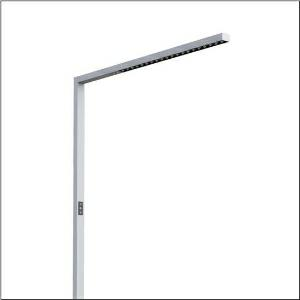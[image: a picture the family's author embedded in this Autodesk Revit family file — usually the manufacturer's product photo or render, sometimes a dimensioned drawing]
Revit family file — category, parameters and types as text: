
# Revit family: silica_31_floor_51my52fa4cs
name_source: partatom
category: Lighting Fixtures
units: mm (PartAtom-declared; Revit-internal decimal feet)

## family parameters
Cut with Voids When Loaded = No
Host = Face
Light Source = No
Part Type = Normal
Room Calculation Point = No
Round Connector Dimension = Use Diameter
Shared = No

## types (1)
- Silica 31 Floor (1 x LED, 10600 lm, 75 W, 4000K)
    Apparent Load = 75 VA
    CIE Flux Codes = 86 100 100 24 100
    Color Rendering = 80
    Color Temperature = 4000K
    Default Elevation = 1800 mm
    Description = Silica® 31 Floor, floorstanding luminaire, secondary optical cover: cover panel, of PMMA, light emission: direct/indirect distribution, primary light characteristic: symmetric, installation type: not mounted, LED, rated luminous flux: 10.600lm, luminous efficacy: 141lm/W, light colour: 840, colour temperature: 4000K, control gear: Touchdim, daylight-dependent control, with cable with plug, mains connection: 230V, AC, 50Hz, connection cable included, cable length: 2,5m, rated input power: 75W, luminaire head, of aluminium, metallic grey (RAL 9006), length: 1.203mm, width: 52mm, supporting column, angular, of aluminium, metallic grey (RAL 9006), baseplate, of steel, metallic grey (RAL 9006), local control - self-sufficient standalone sensors, direct and indirect component separately switchable, protection rating (complete): IP20, insulation class (complete): insulation class I (protective earthing), certification: CE, ENEC, permissible operating ambient temperature: -20..+40°C, standard: EN 50419, packaging unit: 1 piece
    Height = 36 mm
    Lamp = 1 x LED
    Lamp Light Flux = 10600 lm
    Lamp Power = 75 W
    Lamp count = 1
    Length = 1203 mm
    Luminous efficacy = 141 lm/W
    Manufacturer = Siteco
    ModVariant = No
    Model = 51MY52FA4CS
    Mounting Place = Floor
    Mounting Type = Freestanding
    Number of Poles = 1
    OnlyDefault = Yes
    Power Factor = 1
    Product Name = Silica 31 Floor
    Product group = floorstanding luminaire
    ProductGroupID = 1302
    Protection Class = Protection class I
    Protection Degree = IP 20
    RLX_Detail_Level = 1
    RLX_Emergency_Light_Flux = 0 lm
    RLX_Emergency_Type = 0
    RLX_Emergency_Type_DB = No
    RlxData = <blob elided: 19733 chars, md5=68699f00>
    Socket = socket
    Standby Power = 0 W
    System Light Flux = 10600 lm
    System Power = 75 W
    Type Comments = Product without accessories
    Type Image = l_1275303.jpg
    URL = http://relux.com
    VarID = ---
    Voltage = 0 V
    Weight = 0.00 kg
    Width = 52 mm  [stored 0.170604 ft]

note: [stored X ft] marks values corroborated as IEEE doubles in the binary element streams (Revit-internal decimal feet)

## geometry (parser evidence)
native form markers: Blend x4, Sweep x15
no freeform markers — native parametric forms only
